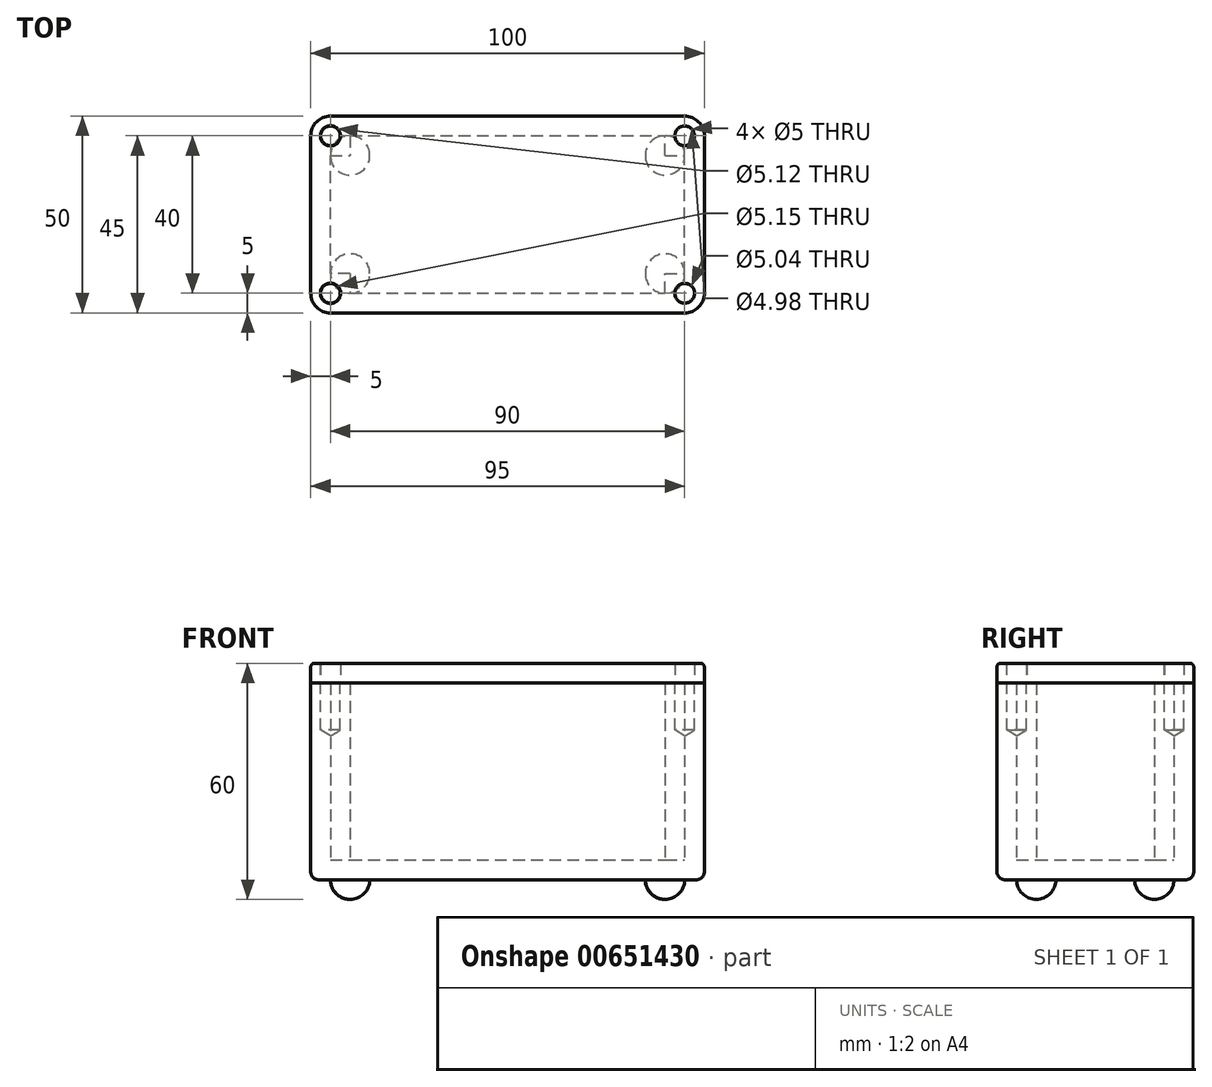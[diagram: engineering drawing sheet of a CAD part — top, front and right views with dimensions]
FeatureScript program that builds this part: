
annotation { "Feature Type Name" : "Feature", "Feature Type Description" : "" }
export const myFeature = defineFeature(function(context is Context, id is Id, definition is map)
    precondition{}
    {
        {
            var Q0;
            Q0=qCreatedBy(makeId("Top.planeOp"),FACE);
            var sketch = newSketch(context, id + "F0", { "sketchPlane" : qUnion([Q0])});
            skLineSegment(sketch, "E0.bottom", {"start": v(0, 0) * mm, "end": v(100, 0) * mm});
            skLineSegment(sketch, "E0.top", {"start": v(0, 50) * mm, "end": v(100, 50) * mm});
            skLineSegment(sketch, "E0.left", {"start": v(0, 0) * mm, "end": v(0, 50) * mm});
            skLineSegment(sketch, "E0.right", {"start": v(100, 0) * mm, "end": v(100, 50) * mm});
            skSolve(sketch);
        }
        {
            var Q0;
            Q0 = qSketchRegion(id + "F0", true);
            extrude(context, id + "F1", {"entities" : qUnion([Q0]), "depth" : 50 * mm, "offsetDistance" : 25 * mm});
        }
        {
            var Q0;
            Q0=makeQuery(id+"F1.opExtrude","CAP_FACE",FACE,{"disambiguationData":[OSD([sQuery(id+"F0.wireOp",EDGE,"E0.bottom"),sQuery(id+"F0.wireOp",EDGE,"E0.top"),sQuery(id+"F0.wireOp",EDGE,"E0.left"),sQuery(id+"F0.wireOp",EDGE,"E0.right")])],"isStart":false});
            var sketch = newSketch(context, id + "F2", { "sketchPlane" : qUnion([Q0])});
            skLineSegment(sketch, "E1.0", {"start": v(5, 45) * mm, "end": v(95, 45) * mm});
            skLineSegment(sketch, "E2.0", {"start": v(5, 5) * mm, "end": v(95, 5) * mm});
            skLineSegment(sketch, "E2.1", {"start": v(5, 5) * mm, "end": v(5, 45) * mm});
            skLineSegment(sketch, "E3.0", {"start": v(95, 5) * mm, "end": v(95, 45) * mm});
            skSolve(sketch);
        }
        {
            var Q0;
            Q0 = qSketchRegion(id + "F2", true);
            extrude(context, id + "F3", {"entities" : qUnion([Q0]), "operationType" : NewBodyOperationType.REMOVE, "oppositeDirection" : true, "depth" : 45 * mm, "offsetDistance" : 25 * mm});
        }
        {
            var Q0;
            Q0=makeQuery(id+"F3.boolean.opBoolean","COPY",FACE,{"derivedFrom":makeQuery(id+"F3.opExtrude","CAP_FACE",FACE,{"disambiguationData":[OSD([sQuery(id+"F2.wireOp",EDGE,"E1.0"),sQuery(id+"F2.wireOp",EDGE,"E2.0"),sQuery(id+"F2.wireOp",EDGE,"E2.1"),sQuery(id+"F2.wireOp",EDGE,"E3.0")])],"isStart":false})});
            var sketch = newSketch(context, id + "F4", { "sketchPlane" : qUnion([Q0])});
            skLineSegment(sketch, "E4.bottom", {"start": v(5, 45) * mm, "end": v(10, 45) * mm});
            skLineSegment(sketch, "E4.top", {"start": v(5, 40) * mm, "end": v(10, 40) * mm});
            skLineSegment(sketch, "E4.left", {"start": v(5, 45) * mm, "end": v(5, 40) * mm});
            skLineSegment(sketch, "E4.right", {"start": v(10, 45) * mm, "end": v(10, 40) * mm});
            skLineSegment(sketch, "E5.bottom", {"start": v(10, 10) * mm, "end": v(5, 10) * mm});
            skLineSegment(sketch, "E5.top", {"start": v(10, 5) * mm, "end": v(5, 5) * mm});
            skLineSegment(sketch, "E5.left", {"start": v(10, 10) * mm, "end": v(10, 5) * mm});
            skLineSegment(sketch, "E5.right", {"start": v(5, 10) * mm, "end": v(5, 5) * mm});
            skLineSegment(sketch, "E6.bottom", {"start": v(90, 40) * mm, "end": v(95, 40) * mm});
            skLineSegment(sketch, "E6.top", {"start": v(90, 45) * mm, "end": v(95, 45) * mm});
            skLineSegment(sketch, "E6.left", {"start": v(90, 40) * mm, "end": v(90, 45) * mm});
            skLineSegment(sketch, "E6.right", {"start": v(95, 40) * mm, "end": v(95, 45) * mm});
            skLineSegment(sketch, "E7.bottom", {"start": v(90, 5) * mm, "end": v(95, 5) * mm});
            skLineSegment(sketch, "E7.top", {"start": v(90, 10) * mm, "end": v(95, 10) * mm});
            skLineSegment(sketch, "E7.left", {"start": v(90, 5) * mm, "end": v(90, 10) * mm});
            skLineSegment(sketch, "E7.right", {"start": v(95, 5) * mm, "end": v(95, 10) * mm});
            skSolve(sketch);
        }
        {
            var Q0;
            Q0 = qSketchRegion(id + "F4", true);
            extrude(context, id + "F5", {"entities" : qUnion([Q0]), "operationType" : NewBodyOperationType.ADD, "depth" : 45 * mm, "offsetDistance" : 25 * mm});
        }
        {
            var Q0;
            Q0=makeQuery(id+"F5.boolean.opBoolean","MERGE",FACE,{"derivedFrom":[makeQuery(id+"F1.opExtrude","CAP_FACE",FACE,{"disambiguationData":[OSD([sQuery(id+"F0.wireOp",EDGE,"E0.bottom"),sQuery(id+"F0.wireOp",EDGE,"E0.top"),sQuery(id+"F0.wireOp",EDGE,"E0.left"),sQuery(id+"F0.wireOp",EDGE,"E0.right")])],"isStart":false}),makeQuery(id+"F5.opExtrude","CAP_FACE",FACE,{"disambiguationData":[OSD([sQuery(id+"F4.wireOp",EDGE,"E4.bottom"),sQuery(id+"F4.wireOp",EDGE,"E4.top"),sQuery(id+"F4.wireOp",EDGE,"E4.left"),sQuery(id+"F4.wireOp",EDGE,"E4.right")])],"isStart":false}),makeQuery(id+"F5.opExtrude","CAP_FACE",FACE,{"disambiguationData":[OSD([sQuery(id+"F4.wireOp",EDGE,"E5.bottom"),sQuery(id+"F4.wireOp",EDGE,"E5.top"),sQuery(id+"F4.wireOp",EDGE,"E5.left"),sQuery(id+"F4.wireOp",EDGE,"E5.right")])],"isStart":false}),makeQuery(id+"F5.opExtrude","CAP_FACE",FACE,{"disambiguationData":[OSD([sQuery(id+"F4.wireOp",EDGE,"E6.bottom"),sQuery(id+"F4.wireOp",EDGE,"E6.top"),sQuery(id+"F4.wireOp",EDGE,"E6.left"),sQuery(id+"F4.wireOp",EDGE,"E6.right")])],"isStart":false}),makeQuery(id+"F5.opExtrude","CAP_FACE",FACE,{"disambiguationData":[OSD([sQuery(id+"F4.wireOp",EDGE,"E7.bottom"),sQuery(id+"F4.wireOp",EDGE,"E7.top"),sQuery(id+"F4.wireOp",EDGE,"E7.left"),sQuery(id+"F4.wireOp",EDGE,"E7.right")])],"isStart":false})]});
            var sketch = newSketch(context, id + "F6", { "sketchPlane" : qUnion([Q0])});
            skPoint(sketch, "E8", {"position": v(5, 45) * mm});
            skPoint(sketch, "E9", {"position": v(5, 5) * mm});
            skPoint(sketch, "E10", {"position": v(95, 5) * mm});
            skPoint(sketch, "E11", {"position": v(95, 45) * mm});
            skSolve(sketch);
        }
        {
            var Q0;
            Q0=sQuery(id+"F6.wireOp",VERTEX,"E8");
            var Q1;
            Q1=sQuery(id+"F6.wireOp",VERTEX,"E9");
            var Q2;
            Q2=sQuery(id+"F6.wireOp",VERTEX,"E10");
            var Q3;
            Q3=sQuery(id+"F6.wireOp",VERTEX,"E11");
            var Q4;
            Q4=makeQuery(id+"F1.opExtrude","SWEPT_BODY",BODY,{"disambiguationData":[OSD([sQuery(id+"F0.wireOp",EDGE,"E0.bottom"),sQuery(id+"F0.wireOp",EDGE,"E0.top"),sQuery(id+"F0.wireOp",EDGE,"E0.left"),sQuery(id+"F0.wireOp",EDGE,"E0.right")])]});
            hole(context, id + "F7", {"style" : HoleStyle.SIMPLE, "endStyle" : HoleEndStyle.BLIND, "holeDiameter" : 5 * mm, "majorDiameter" : 5 * mm, "holeDepth" : 12 * mm, "isTappedThrough" : true, "tappedDepth" : 12 * mm, "tapClearance" : 3, "locations" : qUnion([Q0, Q1, Q2, Q3]), "scope" : qUnion([Q4])});
        }
        {
            var Q0;
            Q0=makeQuery(id+"F1.opExtrude","SWEPT_EDGE",EDGE,{"disambiguationData":[OSD([sQuery(id+"F0.wireOp",EDGE,"E0.bottom"),sQuery(id+"F0.wireOp",EDGE,"E0.left")])]});
            var Q1;
            Q1=makeQuery(id+"F1.opExtrude","SWEPT_EDGE",EDGE,{"disambiguationData":[OSD([sQuery(id+"F0.wireOp",EDGE,"E0.top"),sQuery(id+"F0.wireOp",EDGE,"E0.left")])]});
            var Q2;
            Q2=makeQuery(id+"F1.opExtrude","SWEPT_EDGE",EDGE,{"disambiguationData":[OSD([sQuery(id+"F0.wireOp",EDGE,"E0.top"),sQuery(id+"F0.wireOp",EDGE,"E0.right")])]});
            var Q3;
            Q3=makeQuery(id+"F1.opExtrude","SWEPT_EDGE",EDGE,{"disambiguationData":[OSD([sQuery(id+"F0.wireOp",EDGE,"E0.bottom"),sQuery(id+"F0.wireOp",EDGE,"E0.right")])]});
            fillet(context, id + "F8", {"entities" : qUnion([Q0, Q1, Q2, Q3]), "radius" : 5 * mm, "tangentPropagation" : true, "allowEdgeOverflow" : false});
        }
        {
            var Q0;
            Q0=makeQuery(id+"F5.boolean.opBoolean","MERGE",FACE,{"derivedFrom":[makeQuery(id+"F1.opExtrude","CAP_FACE",FACE,{"disambiguationData":[OSD([sQuery(id+"F0.wireOp",EDGE,"E0.bottom"),sQuery(id+"F0.wireOp",EDGE,"E0.top"),sQuery(id+"F0.wireOp",EDGE,"E0.left"),sQuery(id+"F0.wireOp",EDGE,"E0.right")])],"isStart":false}),makeQuery(id+"F5.opExtrude","CAP_FACE",FACE,{"disambiguationData":[OSD([sQuery(id+"F4.wireOp",EDGE,"E4.bottom"),sQuery(id+"F4.wireOp",EDGE,"E4.top"),sQuery(id+"F4.wireOp",EDGE,"E4.left"),sQuery(id+"F4.wireOp",EDGE,"E4.right")])],"isStart":false}),makeQuery(id+"F5.opExtrude","CAP_FACE",FACE,{"disambiguationData":[OSD([sQuery(id+"F4.wireOp",EDGE,"E5.bottom"),sQuery(id+"F4.wireOp",EDGE,"E5.top"),sQuery(id+"F4.wireOp",EDGE,"E5.left"),sQuery(id+"F4.wireOp",EDGE,"E5.right")])],"isStart":false}),makeQuery(id+"F5.opExtrude","CAP_FACE",FACE,{"disambiguationData":[OSD([sQuery(id+"F4.wireOp",EDGE,"E6.bottom"),sQuery(id+"F4.wireOp",EDGE,"E6.top"),sQuery(id+"F4.wireOp",EDGE,"E6.left"),sQuery(id+"F4.wireOp",EDGE,"E6.right")])],"isStart":false}),makeQuery(id+"F5.opExtrude","CAP_FACE",FACE,{"disambiguationData":[OSD([sQuery(id+"F4.wireOp",EDGE,"E7.bottom"),sQuery(id+"F4.wireOp",EDGE,"E7.top"),sQuery(id+"F4.wireOp",EDGE,"E7.left"),sQuery(id+"F4.wireOp",EDGE,"E7.right")])],"isStart":false})]});
            var sketch = newSketch(context, id + "F9", { "sketchPlane" : qUnion([Q0])});
            skLineSegment(sketch, "E12.bottom", {"start": v(5, 50) * mm, "end": v(95, 50) * mm});
            skLineSegment(sketch, "E12.top", {"start": v(5, 0) * mm, "end": v(95, 0) * mm});
            skLineSegment(sketch, "E12.left", {"start": v(0, 45) * mm, "end": v(0, 5) * mm});
            skLineSegment(sketch, "E12.right", {"start": v(100, 45) * mm, "end": v(100, 5) * mm});
            skPoint(sketch, "E13", {"position": v(5, 50) * mm});
            skPoint(sketch, "E14", {"position": v(65.6, 27.38) * mm});
            skPoint(sketch, "E15", {"position": v(5, 5) * mm});
            skPoint(sketch, "E16", {"position": v(95, 5) * mm});
            skPoint(sketch, "E17", {"position": v(95, 45) * mm});
            skCircle(sketch, "E18", {"center": v(95, 45) * mm, "radius": 2.5 * mm});
            skCircle(sketch, "E19", {"center": v(95, 5) * mm, "radius": 2.52 * mm});
            skCircle(sketch, "E20", {"center": v(5, 5) * mm, "radius": 2.58 * mm});
            skCircle(sketch, "E21", {"center": v(5, 45) * mm, "radius": 2.56 * mm});
            skPoint(sketch, "E22.visualSharp", {"position": v(0, 50) * mm});
            skArc(sketch, "E22.filletArc", {"start": v(5, 50) * mm, "mid": v(1.46, 48.54) * mm, "end": v(0, 45) * mm});
            skPoint(sketch, "E23.visualSharp", {"position": v(0, 0) * mm});
            skArc(sketch, "E23.filletArc", {"start": v(0, 5) * mm, "mid": v(1.46, 1.46) * mm, "end": v(5, 0) * mm});
            skPoint(sketch, "E24.visualSharp", {"position": v(100, 0) * mm});
            skArc(sketch, "E24.filletArc", {"start": v(95, 0) * mm, "mid": v(98.54, 1.46) * mm, "end": v(100, 5) * mm});
            skPoint(sketch, "E25.visualSharp", {"position": v(100, 50) * mm});
            skArc(sketch, "E25.filletArc", {"start": v(100, 45) * mm, "mid": v(98.54, 48.54) * mm, "end": v(95, 50) * mm});
            skSolve(sketch);
        }
        {
            var Q0;
            Q0 = qSketchRegion(id + "F9", true);
            extrude(context, id + "F10", {"entities" : qUnion([Q0]), "depth" : 5 * mm, "offsetDistance" : 25 * mm});
        }
        {
            var Q0;
            Q0=makeQuery(id+"F1.opExtrude","CAP_FACE",FACE,{"disambiguationData":[OSD([sQuery(id+"F0.wireOp",EDGE,"E0.bottom"),sQuery(id+"F0.wireOp",EDGE,"E0.top"),sQuery(id+"F0.wireOp",EDGE,"E0.left"),sQuery(id+"F0.wireOp",EDGE,"E0.right")])],"isStart":true});
            var sketch = newSketch(context, id + "F11", { "sketchPlane" : qUnion([Q0])});
            skCircle(sketch, "E26", {"center": v(10, -10) * mm, "radius": 5 * mm});
            skCircle(sketch, "E27", {"center": v(90, -10) * mm, "radius": 5 * mm});
            skCircle(sketch, "E28", {"center": v(90, -40) * mm, "radius": 5 * mm});
            skCircle(sketch, "E29", {"center": v(10, -40) * mm, "radius": 5 * mm});
            skSolve(sketch);
        }
        {
            var Q0;
            Q0 = qSketchRegion(id + "F11", true);
            extrude(context, id + "F12", {"entities" : qUnion([Q0]), "operationType" : NewBodyOperationType.ADD, "depth" : 5 * mm, "offsetDistance" : 25 * mm});
        }
        {
            var Q0;
            Q0=makeQuery(id+"F12.opExtrude","CAP_FACE",FACE,{"disambiguationData":[OSD([sQuery(id+"F11.wireOp",EDGE,"E26")])],"isStart":false});
            var Q1;
            Q1=makeQuery(id+"F12.opExtrude","CAP_FACE",FACE,{"disambiguationData":[OSD([sQuery(id+"F11.wireOp",EDGE,"E29")])],"isStart":false});
            var Q2;
            Q2=makeQuery(id+"F12.opExtrude","CAP_FACE",FACE,{"disambiguationData":[OSD([sQuery(id+"F11.wireOp",EDGE,"E27")])],"isStart":false});
            var Q3;
            Q3=makeQuery(id+"F12.opExtrude","CAP_FACE",FACE,{"disambiguationData":[OSD([sQuery(id+"F11.wireOp",EDGE,"E28")])],"isStart":false});
            fillet(context, id + "F13", {"entities" : qUnion([Q0, Q1, Q2, Q3]), "radius" : 5 * mm, "tangentPropagation" : true, "allowEdgeOverflow" : false});
        }
        {
            var Q0;
            Q0=makeQuery(id+"F1.opExtrude","CAP_EDGE",EDGE,{"disambiguationData":[OSD([sQuery(id+"F0.wireOp",EDGE,"E0.left")])],"isStart":true});
            fillet(context, id + "F14", {"entities" : qUnion([Q0]), "radius" : 2 * mm, "tangentPropagation" : true, "allowEdgeOverflow" : false});
        }
        {
            var Q0;
            Q0=makeQuery(id+"F10.opExtrude","CAP_EDGE",EDGE,{"disambiguationData":[OSD([sQuery(id+"F9.wireOp",EDGE,"E12.bottom")])],"isStart":false});
            fillet(context, id + "F15", {"entities" : qUnion([Q0]), "radius" : 1 * mm, "tangentPropagation" : true, "allowEdgeOverflow" : false});
        }
    });
